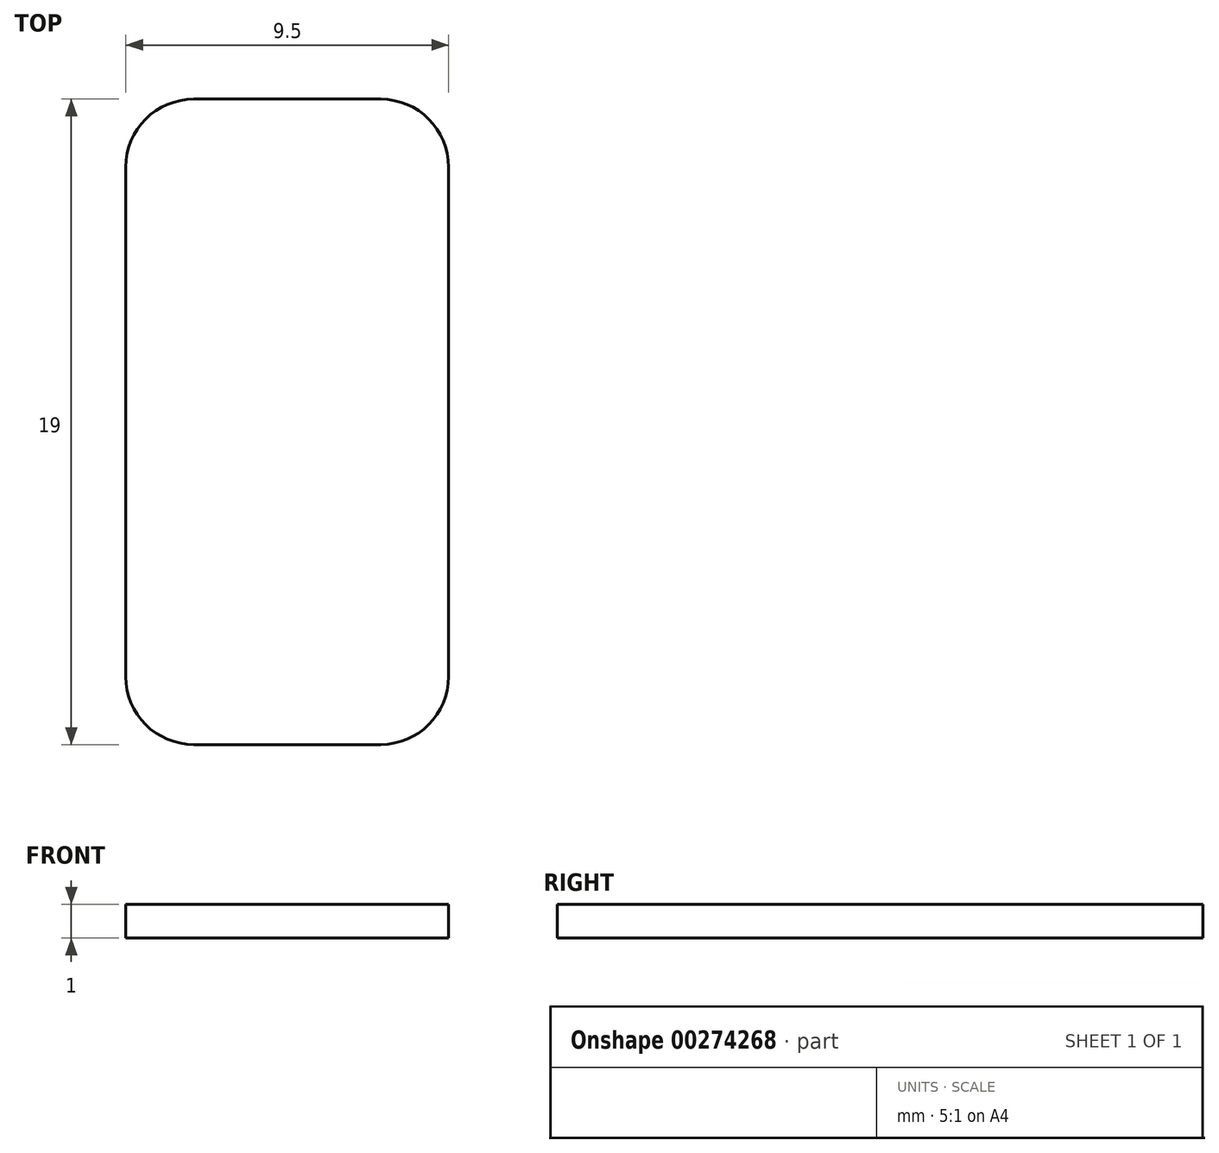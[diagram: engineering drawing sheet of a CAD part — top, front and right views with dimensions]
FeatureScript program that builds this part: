
annotation { "Feature Type Name" : "Feature", "Feature Type Description" : "" }
export const myFeature = defineFeature(function(context is Context, id is Id, definition is map)
    precondition{}
    {
        {
            var Q0;
            Q0=qCreatedBy(makeId("Top.planeOp"),FACE);
            var sketch = newSketch(context, id + "F0", { "sketchPlane" : qUnion([Q0])});
            skLineSegment(sketch, "E0.bottom", {"start": v(-2.75, 9.5) * mm, "end": v(2.75, 9.5) * mm});
            skLineSegment(sketch, "E0.top", {"start": v(-2.75, -9.5) * mm, "end": v(2.75, -9.5) * mm});
            skLineSegment(sketch, "E0.left", {"start": v(-4.75, 7.5) * mm, "end": v(-4.75, -7.5) * mm});
            skLineSegment(sketch, "E0.right", {"start": v(4.75, 7.5) * mm, "end": v(4.75, -7.5) * mm});
            skPoint(sketch, "E0.middle", {"position": v(0, 0) * mm});
            skPoint(sketch, "E1.visualSharp", {"position": v(-4.75, 9.5) * mm});
            skArc(sketch, "E1.filletArc", {"start": v(-2.75, 9.5) * mm, "mid": v(-4.16, 8.91) * mm, "end": v(-4.75, 7.5) * mm});
            skPoint(sketch, "E2.visualSharp", {"position": v(4.75, 9.5) * mm});
            skArc(sketch, "E2.filletArc", {"start": v(4.75, 7.5) * mm, "mid": v(4.16, 8.91) * mm, "end": v(2.75, 9.5) * mm});
            skPoint(sketch, "E3.visualSharp", {"position": v(4.75, -9.5) * mm});
            skArc(sketch, "E3.filletArc", {"start": v(2.75, -9.5) * mm, "mid": v(4.16, -8.91) * mm, "end": v(4.75, -7.5) * mm});
            skPoint(sketch, "E4.visualSharp", {"position": v(-4.75, -9.5) * mm});
            skArc(sketch, "E4.filletArc", {"start": v(-4.75, -7.5) * mm, "mid": v(-4.16, -8.91) * mm, "end": v(-2.75, -9.5) * mm});
            skSolve(sketch);
        }
        {
            var Q0;
            Q0=makeQuery(id+"F0.imprint","IMPRINT",FACE,{"disambiguationData":[TD([[makeQuery(id+"F0.imprint","IMPRINT",EDGE,{"derivedFrom":sQuery(id+"F0.wireOp",EDGE,"E0.bottom")}),-1.0]])]});
            extrude(context, id + "F1", {"entities" : qUnion([Q0]), "depth" : 1 * mm});
        }
    });
